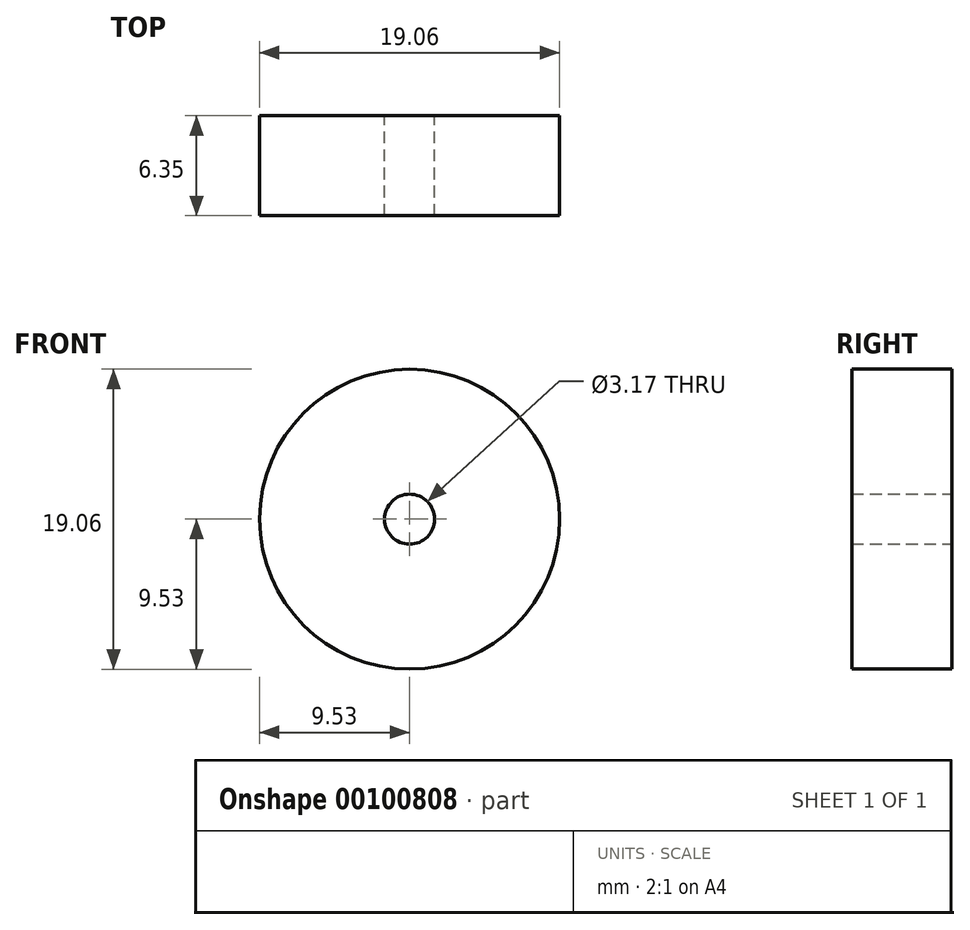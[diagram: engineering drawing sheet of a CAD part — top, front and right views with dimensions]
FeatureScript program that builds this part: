
annotation { "Feature Type Name" : "Feature", "Feature Type Description" : "" }
export const myFeature = defineFeature(function(context is Context, id is Id, definition is map)
    precondition{}
    {
        {
            var Q0;
            Q0=qCreatedBy(makeId("Front.planeOp"),FACE);
            var sketch = newSketch(context, id + "F0", { "sketchPlane" : qUnion([Q0])});
            skCircle(sketch, "E0", {"center": v(0, 0) * mm, "radius": 9.53 * mm});
            skCircle(sketch, "E1", {"center": v(0, 0) * mm, "radius": 1.59 * mm});
            skSolve(sketch);
        }
        {
            var Q0;
            Q0=makeQuery(id+"F0.imprint","IMPRINT",FACE,{"disambiguationData":[TD([[makeQuery(id+"F0.imprint","IMPRINT",EDGE,{"derivedFrom":sQuery(id+"F0.wireOp",EDGE,"E0")}),1.0]])]});
            extrude(context, id + "F1", {"entities" : qUnion([Q0]), "depth" : 6.35 * mm});
        }
    });
